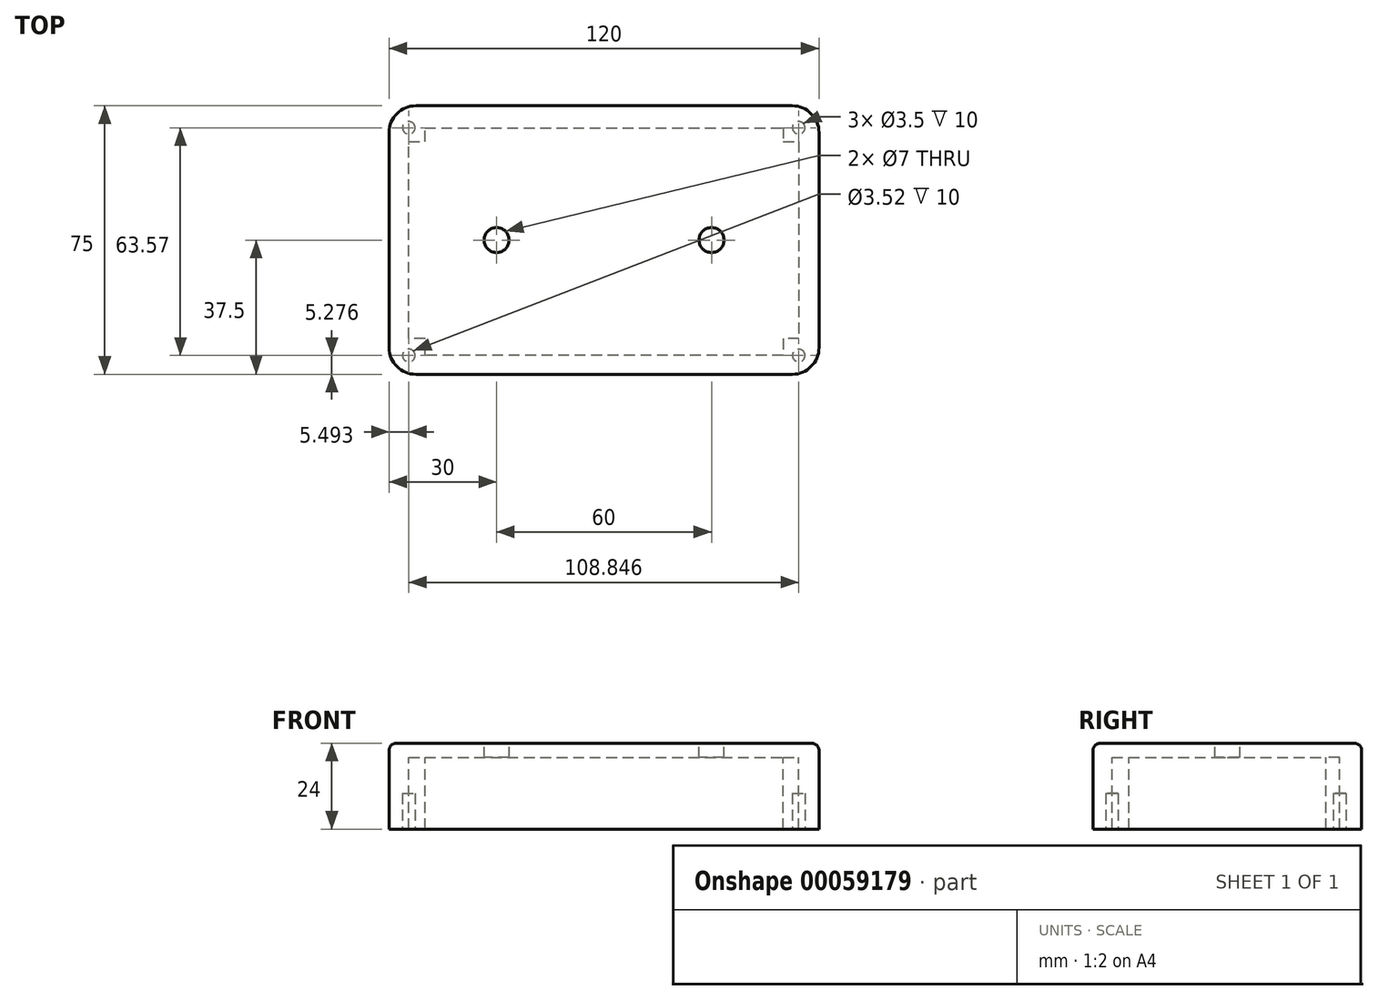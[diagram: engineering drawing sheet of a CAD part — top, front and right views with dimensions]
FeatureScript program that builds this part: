
annotation { "Feature Type Name" : "Feature", "Feature Type Description" : "" }
export const myFeature = defineFeature(function(context is Context, id is Id, definition is map)
    precondition{}
    {
        {
            var Q0;
            Q0=qCreatedBy(makeId("Top.planeOp"),FACE);
            var sketch = newSketch(context, id + "F0", { "sketchPlane" : qUnion([Q0])});
            skLineSegment(sketch, "E0.rect.bottom", {"start": v(60, 37.5) * mm, "end": v(-60, 37.5) * mm});
            skLineSegment(sketch, "E0.rect.top", {"start": v(60, -37.5) * mm, "end": v(-60, -37.5) * mm});
            skLineSegment(sketch, "E0.rect.left", {"start": v(60, 37.5) * mm, "end": v(60, -37.5) * mm});
            skLineSegment(sketch, "E0.rect.right", {"start": v(-60, 37.5) * mm, "end": v(-60, -37.5) * mm});
            skPoint(sketch, "E0.rect.middle", {"position": v(0, 0) * mm});
            skSolve(sketch);
        }
        {
            var Q0;
            Q0=makeQuery(id+"F0.imprint","IMPRINT",FACE,{"disambiguationData":[TD([[makeQuery(id+"F0.imprint","IMPRINT",EDGE,{"derivedFrom":sQuery(id+"F0.wireOp",EDGE,"E0.rect.bottom")}),1.0]])]});
            extrude(context, id + "F1", {"entities" : qUnion([Q0]), "depth" : 4 * mm});
        }
        {
            var Q0;
            Q0=makeQuery(id+"F1.opExtrude","CAP_FACE",FACE,{"disambiguationData":[OSD([sQuery(id+"F0.wireOp",EDGE,"E0.rect.bottom"),sQuery(id+"F0.wireOp",EDGE,"E0.rect.top"),sQuery(id+"F0.wireOp",EDGE,"E0.rect.left"),sQuery(id+"F0.wireOp",EDGE,"E0.rect.right")])],"isStart":true});
            var sketch = newSketch(context, id + "F2", { "sketchPlane" : qUnion([Q0])});
            skLineSegment(sketch, "E1.bottom", {"start": v(60, -37.5) * mm, "end": v(-60, -37.5) * mm});
            skLineSegment(sketch, "E1.top", {"start": v(60, 37.5) * mm, "end": v(-60, 37.5) * mm});
            skLineSegment(sketch, "E1.left", {"start": v(60, -37.5) * mm, "end": v(60, 37.5) * mm});
            skLineSegment(sketch, "E1.right", {"start": v(-60, -37.5) * mm, "end": v(-60, 37.5) * mm});
            skLineSegment(sketch, "E2", {"start": v(50, -37.5) * mm, "end": v(50, 37.5) * mm, "construction": true});
            skLineSegment(sketch, "E3", {"start": v(-50, -37.5) * mm, "end": v(-50, 37.5) * mm, "construction": true});
            skLineSegment(sketch, "E4", {"start": v(60, -27.5) * mm, "end": v(-60, -27.5) * mm, "construction": true});
            skLineSegment(sketch, "E5", {"start": v(60, 27.5) * mm, "end": v(-60, 27.5) * mm, "construction": true});
            skLineSegment(sketch, "E6", {"start": v(50, -27.5) * mm, "end": v(54.34, -27.5) * mm});
            skLineSegment(sketch, "E7", {"start": v(54.34, -27.5) * mm, "end": v(54.34, 27.5) * mm});
            skLineSegment(sketch, "E8", {"start": v(54.34, 27.5) * mm, "end": v(50, 27.5) * mm});
            skLineSegment(sketch, "E9", {"start": v(50, 27.5) * mm, "end": v(50, 32.22) * mm});
            skLineSegment(sketch, "E10", {"start": v(50, 32.22) * mm, "end": v(-50, 32.22) * mm});
            skLineSegment(sketch, "E11", {"start": v(-50, 32.22) * mm, "end": v(-50, 27.5) * mm});
            skLineSegment(sketch, "E12", {"start": v(-50, 27.5) * mm, "end": v(-54.5, 27.5) * mm});
            skLineSegment(sketch, "E13", {"start": v(-54.5, 27.5) * mm, "end": v(-54.5, -27.5) * mm});
            skLineSegment(sketch, "E14", {"start": v(-54.5, -27.5) * mm, "end": v(-50, -27.5) * mm});
            skLineSegment(sketch, "E15", {"start": v(-50, -27.5) * mm, "end": v(-50, -31.35) * mm});
            skLineSegment(sketch, "E16", {"start": v(-50, -31.35) * mm, "end": v(50, -31.35) * mm});
            skLineSegment(sketch, "E17", {"start": v(50, -31.35) * mm, "end": v(50, -27.5) * mm});
            skSolve(sketch);
        }
        {
            var Q0;
            Q0 = qSketchRegion(id + "F2", true);
            extrude(context, id + "F3", {"entities" : qUnion([Q0]), "operationType" : NewBodyOperationType.ADD, "depth" : 20 * mm});
        }
        {
            var Q0;
            Q0=makeQuery(id+"F1.opExtrude","CAP_EDGE",EDGE,{"disambiguationData":[OSD([sQuery(id+"F0.wireOp",EDGE,"E0.rect.left")])],"isStart":false});
            var Q1;
            Q1=makeQuery(id+"F1.opExtrude","CAP_EDGE",EDGE,{"disambiguationData":[OSD([sQuery(id+"F0.wireOp",EDGE,"E0.rect.top")])],"isStart":false});
            var Q2;
            Q2=makeQuery(id+"F1.opExtrude","CAP_EDGE",EDGE,{"disambiguationData":[OSD([sQuery(id+"F0.wireOp",EDGE,"E0.rect.right")])],"isStart":false});
            var Q3;
            Q3=makeQuery(id+"F1.opExtrude","CAP_EDGE",EDGE,{"disambiguationData":[OSD([sQuery(id+"F0.wireOp",EDGE,"E0.rect.bottom")])],"isStart":false});
            fillet(context, id + "F4", {"entities" : qUnion([Q0, Q1, Q2, Q3]), "radius" : 2 * mm, "tangentPropagation" : true, "allowEdgeOverflow" : false});
        }
        {
            var Q0;
            Q0=makeQuery(id+"F3.boolean.opBoolean","MERGE",EDGE,{"derivedFrom":[makeQuery(id+"F1.opExtrude","SWEPT_EDGE",EDGE,{"disambiguationData":[OSD([sQuery(id+"F0.wireOp",EDGE,"E0.rect.top"),sQuery(id+"F0.wireOp",EDGE,"E0.rect.left")])]}),makeQuery(id+"F3.opExtrude","SWEPT_EDGE",EDGE,{"disambiguationData":[OSD([sQuery(id+"F2.wireOp",EDGE,"E1.top"),sQuery(id+"F2.wireOp",EDGE,"E1.left")])]})]});
            var Q1;
            Q1=makeQuery(id+"F3.boolean.opBoolean","MERGE",EDGE,{"derivedFrom":[makeQuery(id+"F1.opExtrude","SWEPT_EDGE",EDGE,{"disambiguationData":[OSD([sQuery(id+"F0.wireOp",EDGE,"E0.rect.bottom"),sQuery(id+"F0.wireOp",EDGE,"E0.rect.left")])]}),makeQuery(id+"F3.opExtrude","SWEPT_EDGE",EDGE,{"disambiguationData":[OSD([sQuery(id+"F2.wireOp",EDGE,"E1.bottom"),sQuery(id+"F2.wireOp",EDGE,"E1.left")])]})]});
            var Q2;
            Q2=makeQuery(id+"F3.boolean.opBoolean","MERGE",EDGE,{"derivedFrom":[makeQuery(id+"F1.opExtrude","SWEPT_EDGE",EDGE,{"disambiguationData":[OSD([sQuery(id+"F0.wireOp",EDGE,"E0.rect.top"),sQuery(id+"F0.wireOp",EDGE,"E0.rect.right")])]}),makeQuery(id+"F3.opExtrude","SWEPT_EDGE",EDGE,{"disambiguationData":[OSD([sQuery(id+"F2.wireOp",EDGE,"E1.top"),sQuery(id+"F2.wireOp",EDGE,"E1.right")])]})]});
            var Q3;
            Q3=makeQuery(id+"F3.boolean.opBoolean","MERGE",EDGE,{"derivedFrom":[makeQuery(id+"F1.opExtrude","SWEPT_EDGE",EDGE,{"disambiguationData":[OSD([sQuery(id+"F0.wireOp",EDGE,"E0.rect.bottom"),sQuery(id+"F0.wireOp",EDGE,"E0.rect.right")])]}),makeQuery(id+"F3.opExtrude","SWEPT_EDGE",EDGE,{"disambiguationData":[OSD([sQuery(id+"F2.wireOp",EDGE,"E1.bottom"),sQuery(id+"F2.wireOp",EDGE,"E1.right")])]})]});
            fillet(context, id + "F5", {"entities" : qUnion([Q0, Q1, Q2, Q3]), "radius" : 7.5 * mm, "tangentPropagation" : true, "allowEdgeOverflow" : false});
        }
        {
            var Q0;
            Q0=makeQuery(id+"F1.opExtrude","CAP_FACE",FACE,{"disambiguationData":[OSD([sQuery(id+"F0.wireOp",EDGE,"E0.rect.bottom"),sQuery(id+"F0.wireOp",EDGE,"E0.rect.top"),sQuery(id+"F0.wireOp",EDGE,"E0.rect.left"),sQuery(id+"F0.wireOp",EDGE,"E0.rect.right")])],"isStart":false});
            var sketch = newSketch(context, id + "F6", { "sketchPlane" : qUnion([Q0])});
            skLineSegment(sketch, "E18", {"start": v(-60, 0) * mm, "end": v(-30, 0) * mm, "construction": true});
            skPoint(sketch, "E18.endSnap0", {"position": v(-60, 0) * mm});
            skLineSegment(sketch, "E19", {"start": v(60, 0) * mm, "end": v(30, 0) * mm, "construction": true});
            skPoint(sketch, "E19.endSnap0", {"position": v(60, 0) * mm});
            skCircle(sketch, "E20", {"center": v(-30, 0) * mm, "radius": 3.5 * mm});
            skCircle(sketch, "E21", {"center": v(30, 0) * mm, "radius": 3.5 * mm});
            skSolve(sketch);
        }
        {
            var Q0;
            Q0 = qSketchRegion(id + "F6", true);
            extrude(context, id + "F7", {"entities" : qUnion([Q0]), "operationType" : NewBodyOperationType.REMOVE, "oppositeDirection" : true, "depth" : 25 * mm});
        }
        {
            var Q0;
            Q0=makeQuery(id+"F3.opExtrude","CAP_FACE",FACE,{"disambiguationData":[OSD([sQuery(id+"F2.wireOp",EDGE,"E1.bottom"),sQuery(id+"F2.wireOp",EDGE,"E1.top"),sQuery(id+"F2.wireOp",EDGE,"E1.left"),sQuery(id+"F2.wireOp",EDGE,"E1.right"),sQuery(id+"F2.wireOp",EDGE,"E6"),sQuery(id+"F2.wireOp",EDGE,"E7"),sQuery(id+"F2.wireOp",EDGE,"E8"),sQuery(id+"F2.wireOp",EDGE,"E9"),sQuery(id+"F2.wireOp",EDGE,"E10"),sQuery(id+"F2.wireOp",EDGE,"E11"),sQuery(id+"F2.wireOp",EDGE,"E12"),sQuery(id+"F2.wireOp",EDGE,"E13"),sQuery(id+"F2.wireOp",EDGE,"E14"),sQuery(id+"F2.wireOp",EDGE,"E15"),sQuery(id+"F2.wireOp",EDGE,"E16"),sQuery(id+"F2.wireOp",EDGE,"E17")])],"isStart":false});
            var sketch = newSketch(context, id + "F8", { "sketchPlane" : qUnion([Q0])});
            skLineSegment(sketch, "E22", {"start": v(-65.78, 32.22) * mm, "end": v(65.26, 32.22) * mm, "construction": true});
            skLineSegment(sketch, "E23", {"start": v(-64.36, -27.5) * mm, "end": v(67.34, -27.5) * mm, "construction": true});
            skLineSegment(sketch, "E24", {"start": v(-54.5, 42.87) * mm, "end": v(-54.5, -47.6) * mm, "construction": true});
            skLineSegment(sketch, "E25", {"start": v(54.34, 44.81) * mm, "end": v(54.34, -43.93) * mm, "construction": true});
            skCircle(sketch, "E26", {"center": v(-54.5, 32.22) * mm, "radius": 1.75 * mm, "construction": true});
            skCircle(sketch, "E27", {"center": v(-54.5, 32.22) * mm, "radius": 1.76 * mm});
            skCircle(sketch, "E28", {"center": v(54.34, 32.22) * mm, "radius": 1.75 * mm});
            skLineSegment(sketch, "E29", {"start": v(-65.71, -31.35) * mm, "end": v(66.48, -31.35) * mm, "construction": true});
            skCircle(sketch, "E30", {"center": v(54.34, -31.35) * mm, "radius": 1.75 * mm});
            skCircle(sketch, "E31", {"center": v(-54.5, -31.35) * mm, "radius": 1.75 * mm});
            skSolve(sketch);
        }
        {
            var Q0;
            Q0 = qSketchRegion(id + "F8", true);
            extrude(context, id + "F9", {"entities" : qUnion([Q0]), "operationType" : NewBodyOperationType.REMOVE, "oppositeDirection" : true, "depth" : 10 * mm});
        }
    });
